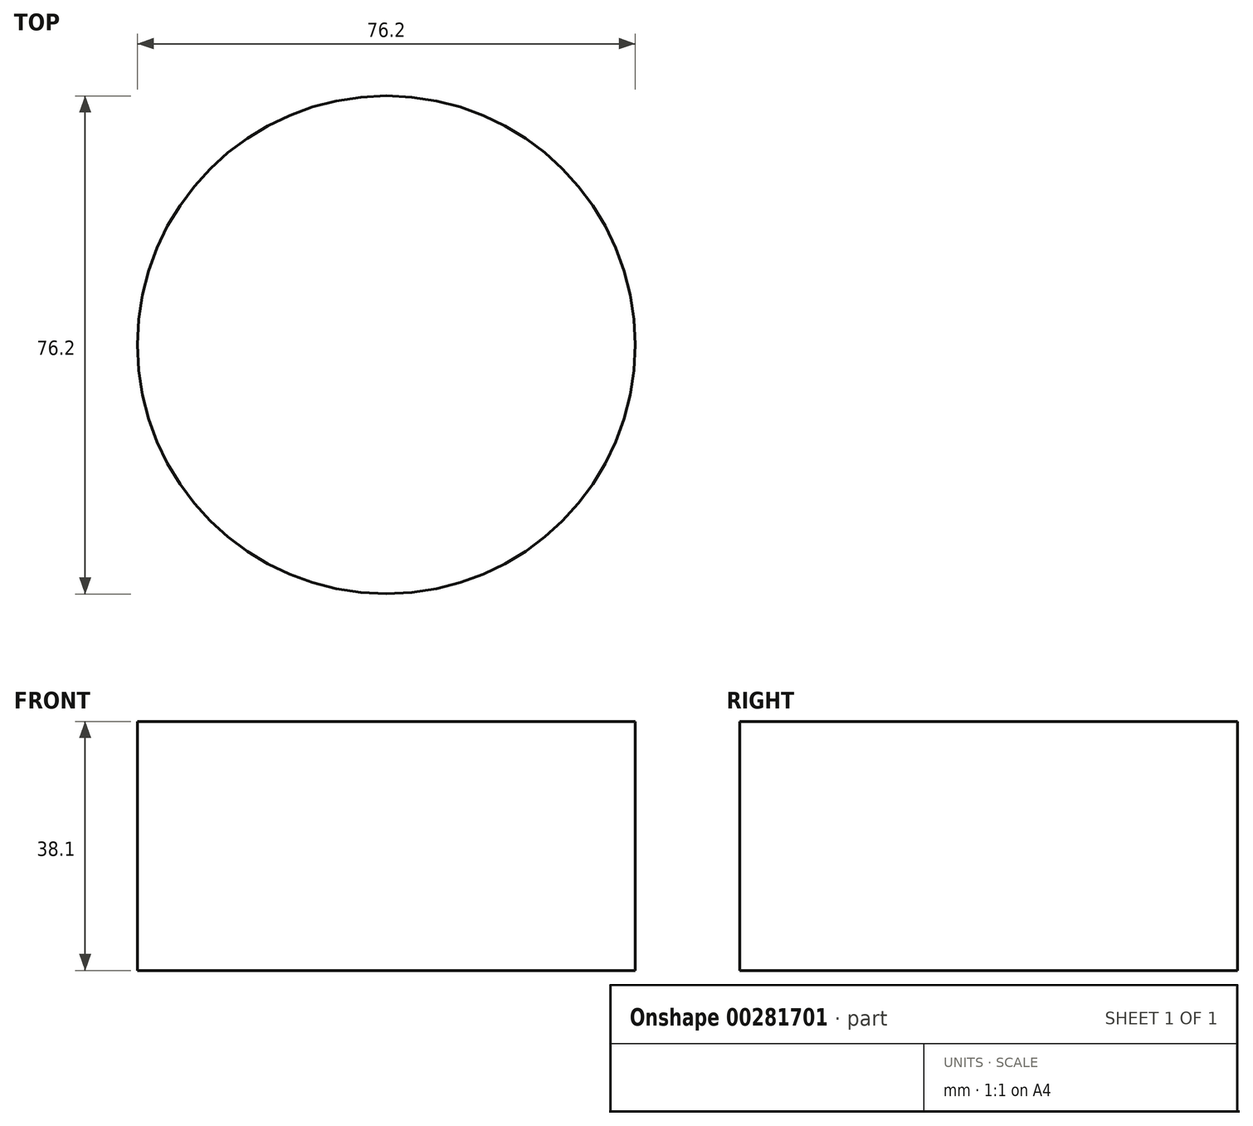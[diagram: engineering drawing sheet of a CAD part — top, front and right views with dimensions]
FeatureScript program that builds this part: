
annotation { "Feature Type Name" : "Feature", "Feature Type Description" : "" }
export const myFeature = defineFeature(function(context is Context, id is Id, definition is map)
    precondition{}
    {
        {
            var Q0;
            Q0=qCreatedBy(makeId("Top.planeOp"),FACE);
            var sketch = newSketch(context, id + "F0", { "sketchPlane" : qUnion([Q0])});
            skCircle(sketch, "E0", {"center": v(4.81, -21.36) * mm, "radius": 38.1 * mm});
            skSolve(sketch);
        }
        {
            var Q0;
            Q0=makeQuery(id+"F0.imprint","IMPRINT",FACE,{"disambiguationData":[TD([[makeQuery(id+"F0.imprint","IMPRINT",EDGE,{"derivedFrom":sQuery(id+"F0.wireOp",EDGE,"E0")}),1.0]])]});
            extrude(context, id + "F1", {"entities" : qUnion([Q0]), "depth" : 38.1 * mm});
        }
    });
